# Revit family: Faucet-Single_Control-American_Standard-Monterrey-611411X_Series
name_source: partatom
category: Plumbing Fixtures
units: mm (PartAtom-declared; Revit-internal decimal feet)

## family parameters
Always vertical = No
Cut with Voids When Loaded = No
OmniClass Number = 23.45.55.14
OmniClass Title = Single Faucets
Part Type = Normal
Room Calculation Point = No
Round Connector Dimension = Use Diameter
Shared = Yes
Work Plane-Based = Yes

## types (5) — shared parameters
ADA Compliant = Yes
Assembly Code = D2020300
CW Connection = No
CWFU = 1.5
Compliance Certifications = These products meet or exceeds:ANSI A117.1,ASME A112.18.1,CSA B 125,NSF 372
Default Elevation = 0"
Finish = Cast Brass-American Standard-002-Polished Chrome
HW Connection = No
HWFU = 1.5
Height = 5 1/8"
Installation Type = Deck Mounted
Length = 4 5/8"
Manufacturer = American Standard
Material = Cast Brass-American Standard-002-Polished Chrome
Pop Up Drain Material = Metal-American Standard-Chrome Plated
Pop Up Drain Width from Faucet Center = 4 5/8"
Pop Up Drain Width from Faucet Center Constraint = 4 5/8"
Pop up Drain Depth = 5"
Price = Prices may vary. Please consult Manufacturer Representative for most up-to-date price list.
Product Documentation Link = https://americanstandard.box.com
Product Page URL = https://www.americanstandard-us.com
Revised Date = 04/29/2022
Tempered Water Connection = Yes
Tempered Water Connection Diameter = 1/2"
Tempered Water Connection Radius = 1/4"
URL = http://www.americanstandard-us.com
Vent Connection = No
WFU = 2
Waste Connection = No
Width = 5 13/16"

## per-type parameters (varying)
| type | Description | Flow Rate | Less drain, less pop-up hole & rod | Metal pop-up drain |
| 6114.110.002 | Monterrey® Cast 4-Inch Centerset Single-Handle Faucet 1.5 gpm/5.7 Lpm With Metal Pop-Up Drain | 1.5 (5.7L/min) | No | Yes |
| 6114.111.002 | Monterrey® Cast 4-Inch Centerset Single-Handle Faucet 1.5 gpm/5.7 Lpm | 1.5 (5.7L/min) | Yes | No |
| 6114.115.002 | Monterrey® Cast 4-Inch Centerset Single-Handle Faucet 0.5 gpm/1.9 Lpm With Metal Pop-Up Drain | 0.5 (1.9L/min) | No | Yes |
| 6114.116.002 | Monterrey® Cast 4-Inch Centerset Single-Handle Faucet 0.5 gpm/1.9 Lpm | 0.5 (1.9L/min) | Yes | No |
| 6114.114.002 | Monterrey® Cast 4-Inch Centerset Single-Handle Faucet 0.35 gpm/1.3 Lpm | 0.35 (1.3L/min) | Yes | No |

note: column(s) folded — value = type name in every type: Model

## geometry (parser evidence)
native form markers: Sweep x2
no freeform markers — native parametric forms only
